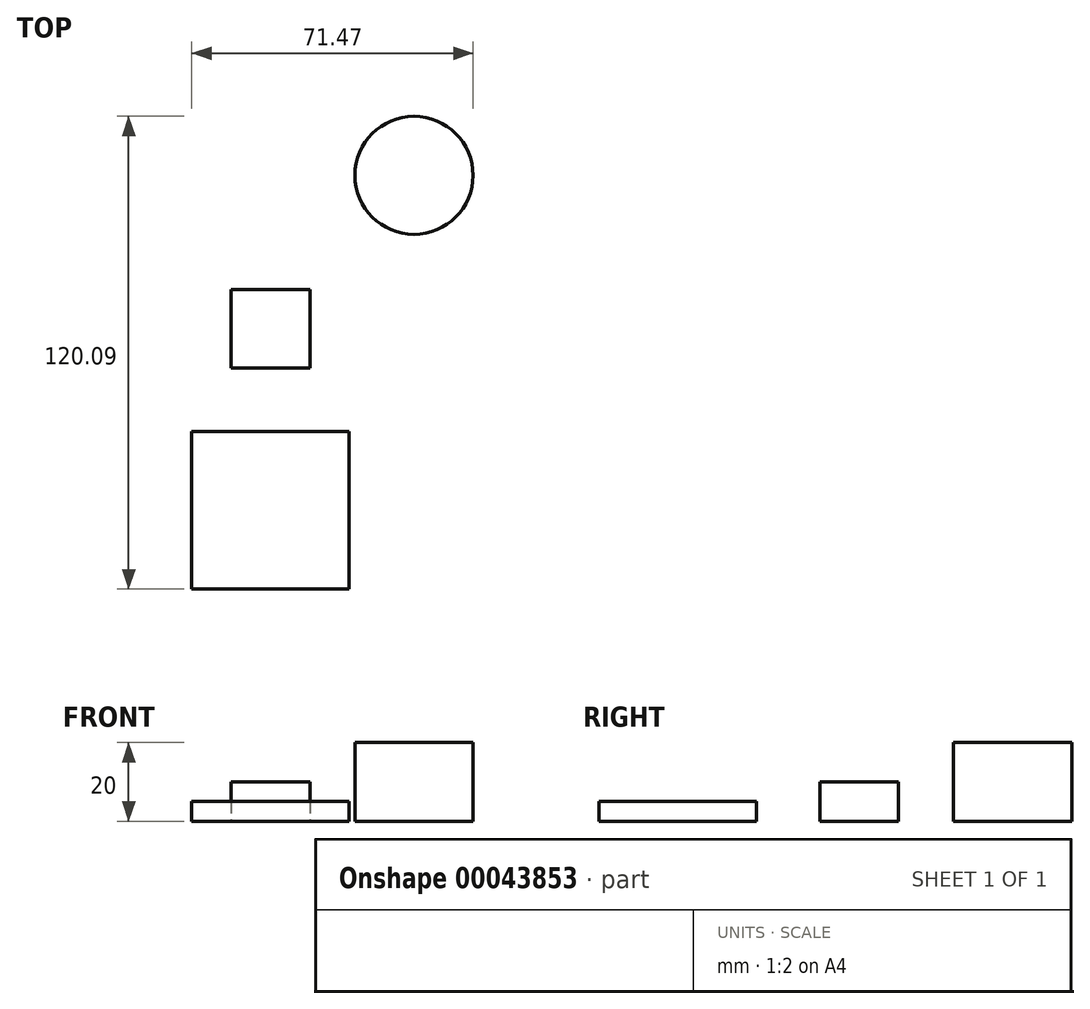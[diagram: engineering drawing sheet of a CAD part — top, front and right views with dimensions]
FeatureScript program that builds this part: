
annotation { "Feature Type Name" : "Feature", "Feature Type Description" : "" }
export const myFeature = defineFeature(function(context is Context, id is Id, definition is map)
    precondition{}
    {
        {
            var Q0;
            Q0=qCreatedBy(makeId("Top.planeOp"),FACE);
            var sketch = newSketch(context, id + "F0", { "sketchPlane" : qUnion([Q0])});
            skLineSegment(sketch, "E0.bottom", {"start": v(10, -10) * mm, "end": v(-10, -10) * mm});
            skLineSegment(sketch, "E0.top", {"start": v(10, 10) * mm, "end": v(-10, 10) * mm});
            skLineSegment(sketch, "E0.left", {"start": v(10, -10) * mm, "end": v(10, 10) * mm});
            skLineSegment(sketch, "E0.right", {"start": v(-10, -10) * mm, "end": v(-10, 10) * mm});
            skPoint(sketch, "E0.middle", {"position": v(0, 0) * mm});
            skSolve(sketch);
        }
        {
            var Q0;
            Q0=makeQuery(id+"F0.imprint","IMPRINT",FACE,{"disambiguationData":[TD([[makeQuery(id+"F0.imprint","IMPRINT",EDGE,{"derivedFrom":sQuery(id+"F0.wireOp",EDGE,"E0.bottom")}),-1.0]])]});
            extrude(context, id + "F1", {"entities" : qUnion([Q0]), "depth" : 10 * mm, "offsetDistance" : 25 * mm});
        }
        {
            var Q0;
            Q0=qCreatedBy(makeId("Top.planeOp"),FACE);
            var sketch = newSketch(context, id + "F2", { "sketchPlane" : qUnion([Q0])});
            skLineSegment(sketch, "E1.bottom", {"start": v(20, -66.12) * mm, "end": v(-20, -66.12) * mm});
            skLineSegment(sketch, "E1.top", {"start": v(20, -26.12) * mm, "end": v(-20, -26.12) * mm});
            skLineSegment(sketch, "E1.left", {"start": v(20, -66.12) * mm, "end": v(20, -26.12) * mm});
            skLineSegment(sketch, "E1.right", {"start": v(-20, -66.12) * mm, "end": v(-20, -26.12) * mm});
            skPoint(sketch, "E1.middle", {"position": v(0, -46.12) * mm});
            skSolve(sketch);
        }
        {
            var Q0;
            Q0=makeQuery(id+"F2.imprint","IMPRINT",FACE,{"disambiguationData":[TD([[makeQuery(id+"F2.imprint","IMPRINT",EDGE,{"derivedFrom":sQuery(id+"F2.wireOp",EDGE,"E1.bottom")}),-1.0]])]});
            extrude(context, id + "F3", {"entities" : qUnion([Q0]), "depth" : 5 * mm, "offsetDistance" : 25 * mm});
        }
        {
            var Q0;
            Q0=qCreatedBy(makeId("Top.planeOp"),FACE);
            var sketch = newSketch(context, id + "F4", { "sketchPlane" : qUnion([Q0])});
            skCircle(sketch, "E2", {"center": v(36.47, 38.97) * mm, "radius": 15 * mm});
            skSolve(sketch);
        }
        {
            var Q0;
            Q0=makeQuery(id+"F4.imprint","IMPRINT",FACE,{"disambiguationData":[TD([[makeQuery(id+"F4.imprint","IMPRINT",EDGE,{"derivedFrom":sQuery(id+"F4.wireOp",EDGE,"E2")}),1.0]])]});
            extrude(context, id + "F5", {"entities" : qUnion([Q0]), "depth" : 20 * mm, "offsetDistance" : 25 * mm});
        }
    });
